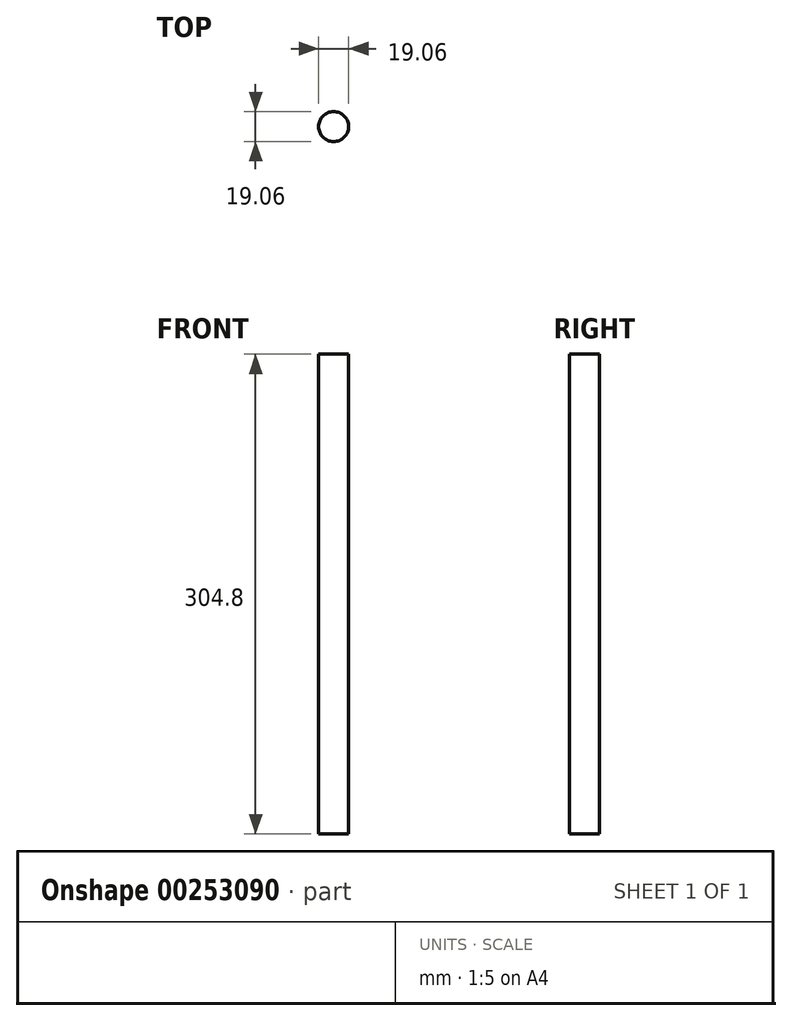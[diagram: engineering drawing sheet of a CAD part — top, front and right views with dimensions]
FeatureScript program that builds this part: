
annotation { "Feature Type Name" : "Feature", "Feature Type Description" : "" }
export const myFeature = defineFeature(function(context is Context, id is Id, definition is map)
    precondition{}
    {
        {
            var Q0;
            Q0=qCreatedBy(makeId("Top.planeOp"),FACE);
            var sketch = newSketch(context, id + "F0", { "sketchPlane" : qUnion([Q0])});
            skCircle(sketch, "E0", {"center": v(0, 0) * mm, "radius": 9.53 * mm});
            skSolve(sketch);
        }
        {
            var Q0;
            Q0=sQuery(id+"F0.wireOp",EDGE,"E0");
            extrude(context, id + "F1", {"bodyType" : ToolBodyType.SURFACE, "surfaceEntities" : qUnion([Q0]), "depth" : 304.8 * mm});
        }
    });
